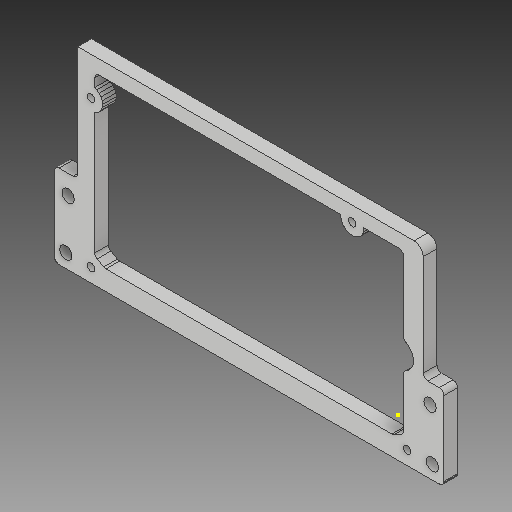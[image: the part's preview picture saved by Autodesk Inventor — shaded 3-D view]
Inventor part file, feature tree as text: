
AUTODESK INVENTOR PART (.ipt)
format: ipt  version: 2018 (Build 220112000, 112)  size: 1,082,880 bytes
history: native  units: mm
features: sketch x10, fillet x9, extrude x7, projected_geometry x3, other x3, hole x2, reference x1
ambient origin geometry x8: Origin, YZ Plane, XZ Plane, XY Plane, X Axis, Y Axis, Z Axis, Center Point
bodies: Solid1 (feature_tree)
feature tree (35):
  extrude  "Extrusion1"  TaperAngle=90.0deg  [1 undecoded]
  extrude  "Extrusion2"  Depth=2.0mm
  fillet  "Fillet1"  Radius=2.0mm
  fillet  "Fillet2"  Radius=2.0mm
  fillet  "Fillet3"  Radius=2.0mm
  fillet  "Fillet4"  Radius=2.0mm
  fillet  "Fillet5"  [1 undecoded]
  extrude  "Extrusion3"  Depth=10.0mm TaperAngle=0.0deg
  fillet  "Fillet6"  Radius=2.0mm
  extrude  "Extrusion4"  Depth=2.0mm
  fillet  "Fillet7"  Radius=10.0mm
  hole  "Hole1"  [1 undecoded]
  hole  "Hole2"  [1 undecoded]
  extrude  "Extrusion5"  [1 undecoded]
  fillet  "Fillet8"  [1 undecoded]
  sketch  "Sketch9"  dims[d39=6.0mm d40=0.0mm d41=2.0mm]
  extrude  "Extrusion6"  [1 undecoded]
  extrude  "Extrusion7"  [1 undecoded]
  fillet  "Fillet9"  [1 undecoded]
  sketch  "Sketch1"  dims[d0=6.0mm d1=0.0mm d3=90.0deg]
  sketch  "Sketch2"  dims[d5=6.0mm d6=0.0mm d7=2.0mm d8=2.0mm d9=2.0mm d10=2.0mm d11=2.0mm d12=90.0deg]
  sketch  "Sketch3"  dims[d13=90.0deg d14=10.0mm d15=0.0mm d16=2.0mm]
  sketch  "Sketch4"  dims[d17=10.0mm d18=0.0mm d19=2.0mm]
  sketch  "Sketch5"  dims[d20=3.3mm d21=6.0mm d22=4.0mm d23=2.0mm d24=90.0deg d25=8.0mm d26=20.594885mm]
  projected_geometry  "Projected Loop2"
  sketch  "Sketch6"  dims[d27=5.4mm d28=6.0mm d29=4.0mm d30=2.0mm d31=90.0deg d32=8.0mm d33=20.594885mm d34=10.0mm d35=0.0mm]
  projected_geometry  "Projected Loop3"
  sketch  "Sketch7"  dims[d36=4.0mm d37=6.0mm d38=0.0mm]
  projected_geometry  "Projected Loop4"
  sketch  "Sketch10"
  sketch  "Sketch11"
  reference  "Reference3"
  parser-record x1  (decoder bookkeeping rows leaked as tree rows — omitted from the tree; the rows remain in map.json)
  other  "PSU.iam"
  other  "power supply:1"
note: 9 required parameter values undecoded (feature->parameter linkage not recoverable at this tier; creation-order binding heuristic only, values carry confidence <= 0.55)
note: 1 file-system path scrubbed to <path> (originals preserved in map.json)
